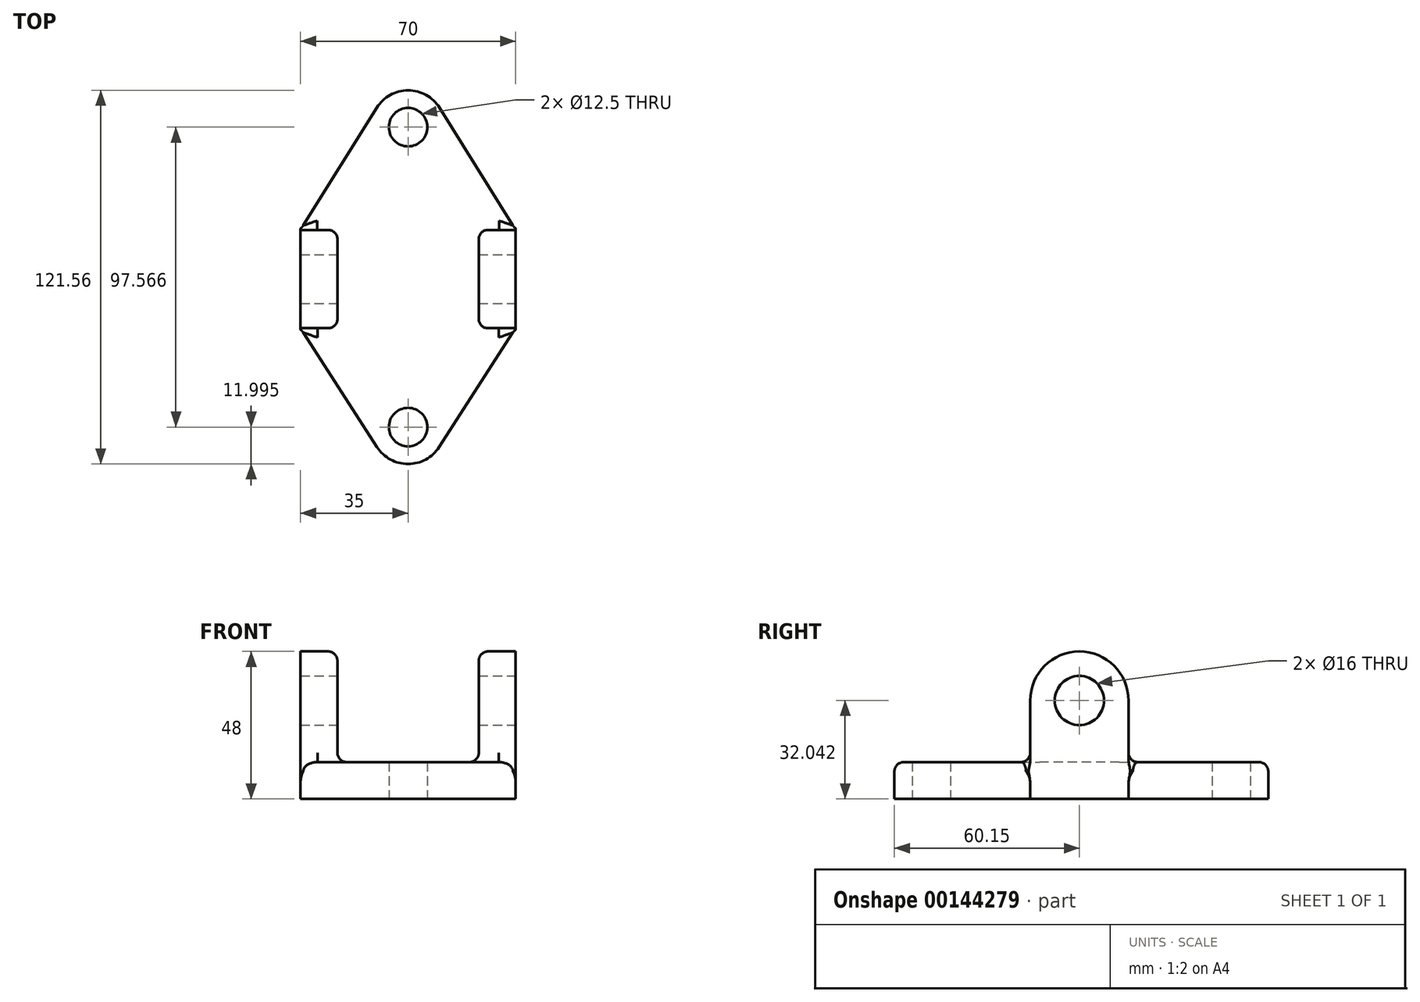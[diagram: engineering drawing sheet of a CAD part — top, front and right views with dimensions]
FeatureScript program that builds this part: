
annotation { "Feature Type Name" : "Feature", "Feature Type Description" : "" }
export const myFeature = defineFeature(function(context is Context, id is Id, definition is map)
    precondition{}
    {
        {
            var Q0;
            Q0=qCreatedBy(makeId("Right.planeOp"),FACE);
            var sketch = newSketch(context, id + "F0", { "sketchPlane" : qUnion([Q0])});
            skLineSegment(sketch, "E0", {"start": v(-16, 0) * mm, "end": v(-16, 32) * mm});
            skLineSegment(sketch, "E1", {"start": v(-16, 0) * mm, "end": v(16, 0) * mm});
            skLineSegment(sketch, "E2", {"start": v(16, 0) * mm, "end": v(16, 32) * mm});
            skCircle(sketch, "E3", {"center": v(0, 32) * mm, "radius": 6 * mm});
            skArc(sketch, "E4", {"start": v(16, 32) * mm, "mid": v(0, 48) * mm, "end": v(-16, 32) * mm});
            skSolve(sketch);
        }
        {
            var Q0;
            Q0 = qSketchRegion(id + "F0", true);
            extrude(context, id + "F1", {"entities" : qUnion([Q0]), "oppositeDirection" : true, "depth" : 12 * mm});
        }
        {
            var Q0;
            Q0=qCreatedBy(makeId("Top.planeOp"),FACE);
            var sketch = newSketch(context, id + "F2", { "sketchPlane" : qUnion([Q0])});
            skPoint(sketch, "E5.0", {"position": v(-12, 16) * mm});
            skPoint(sketch, "E6.0", {"position": v(-12, -16) * mm});
            skCircle(sketch, "E7", {"center": v(23, 49.41) * mm, "radius": 6.25 * mm});
            skArc(sketch, "E8", {"start": v(33.18, 55.77) * mm, "mid": v(23, 61.41) * mm, "end": v(12.82, 55.77) * mm});
            skLineSegment(sketch, "E9", {"start": v(33.18, 55.77) * mm, "end": v(58, 16) * mm});
            skPoint(sketch, "E10", {"position": v(-12, 0) * mm});
            skPoint(sketch, "E11", {"position": v(58, 0) * mm});
            skLineSegment(sketch, "E12", {"start": v(58, 0) * mm, "end": v(58, -16) * mm});
            skLineSegment(sketch, "E13", {"start": v(58, -16) * mm, "end": v(58, 16) * mm});
            skPoint(sketch, "E14", {"position": v(23, 0) * mm});
            skLineSegment(sketch, "E15", {"start": v(23, 74.76) * mm, "end": v(23, -48.15) * mm, "construction": true});
            skLineSegment(sketch, "E16", {"start": v(-12, 16) * mm, "end": v(12.82, 55.77) * mm});
            skCircle(sketch, "E17", {"center": v(23, -48.15) * mm, "radius": 6.25 * mm});
            skArc(sketch, "E18", {"start": v(12.91, -54.66) * mm, "mid": v(23, -60.15) * mm, "end": v(33.09, -54.66) * mm});
            skLineSegment(sketch, "E19", {"start": v(58, -16) * mm, "end": v(33.09, -54.66) * mm});
            skLineSegment(sketch, "E20", {"start": v(12.91, -54.66) * mm, "end": v(-12, -16) * mm});
            skLineSegment(sketch, "E21", {"start": v(-12, -16) * mm, "end": v(-12, 16) * mm});
            skSolve(sketch);
        }
        {
            var Q0;
            Q0 = qSketchRegion(id + "F2", true);
            extrude(context, id + "F3", {"entities" : qUnion([Q0]), "operationType" : NewBodyOperationType.ADD, "depth" : 12 * mm});
        }
        {
            var Q0;
            Q0=makeQuery(id+"F3.opExtrude","SWEPT_FACE",FACE,{"disambiguationData":[OSD([sQuery(id+"F2.wireOp",EDGE,"E13")])]});
            var sketch = newSketch(context, id + "F4", { "sketchPlane" : qUnion([Q0])});
            skLineSegment(sketch, "E22.0.0", {"start": v(-16, 0) * mm, "end": v(-16, 12) * mm});
            skLineSegment(sketch, "E22.0.1", {"start": v(-16, 12) * mm, "end": v(-16, 32) * mm});
            skArc(sketch, "E22.0.2", {"start": v(-16, 32) * mm, "mid": v(0, 48) * mm, "end": v(16, 32) * mm});
            skLineSegment(sketch, "E22.0.3", {"start": v(16, 32) * mm, "end": v(16, 12) * mm});
            skLineSegment(sketch, "E22.0.4", {"start": v(16, 12) * mm, "end": v(16, 0) * mm});
            skLineSegment(sketch, "E22.0.5", {"start": v(16, 0) * mm, "end": v(-16, 0) * mm});
            skCircle(sketch, "E23.0", {"center": v(0, 32) * mm, "radius": 6 * mm});
            skSolve(sketch);
        }
        {
            var Q0;
            Q0 = qSketchRegion(id + "F4", true);
            extrude(context, id + "F5", {"entities" : qUnion([Q0]), "operationType" : NewBodyOperationType.ADD, "oppositeDirection" : true, "depth" : 12 * mm});
        }
        {
            var Q0;
            Q0=makeQuery(id+"F3.opExtrude","CAP_EDGE",EDGE,{"disambiguationData":[OSD([sQuery(id+"F2.wireOp",EDGE,"E19")])],"isStart":false});
            var Q1;
            Q1=makeQuery(id+"F3.opExtrude","CAP_EDGE",EDGE,{"disambiguationData":[OSD([sQuery(id+"F2.wireOp",EDGE,"E9")])],"isStart":false});
            var Q2;
            Q2=makeQuery(id+"F5.opExtrude","CAP_EDGE",EDGE,{"disambiguationData":[OSD([sQuery(id+"F4.wireOp",EDGE,"E22.0.2")])],"isStart":false});
            var Q3;
            Q3=makeQuery(id+"F1.opExtrude","CAP_EDGE",EDGE,{"disambiguationData":[OSD([sQuery(id+"F0.wireOp",EDGE,"E4")])],"isStart":true});
            fillet(context, id + "F6", {"entities" : qUnion([Q0, Q1, Q2, Q3]), "radius" : 3 * mm, "tangentPropagation" : true, "allowEdgeOverflow" : false});
        }
        {
            var Q0;
            Q0=makeQuery(id+"F5.boolean.opBoolean","INTERSECT",EDGE,{"derivedFrom":[makeQuery(id+"F3.opExtrude","CAP_FACE",FACE,{"disambiguationData":[OSD([sQuery(id+"F2.wireOp",EDGE,"E7"),sQuery(id+"F2.wireOp",EDGE,"E8"),sQuery(id+"F2.wireOp",EDGE,"E9"),sQuery(id+"F2.wireOp",EDGE,"E13"),sQuery(id+"F2.wireOp",EDGE,"E16"),sQuery(id+"F2.wireOp",EDGE,"E17"),sQuery(id+"F2.wireOp",EDGE,"E18"),sQuery(id+"F2.wireOp",EDGE,"E19"),sQuery(id+"F2.wireOp",EDGE,"E20"),sQuery(id+"F2.wireOp",EDGE,"E21")])],"isStart":false}),makeQuery(id+"F5.opExtrude","SWEPT_FACE",FACE,{"disambiguationData":[OSD([sQuery(id+"F4.wireOp",EDGE,"E22.0.0"),sQuery(id+"F4.wireOp",EDGE,"E22.0.1")])]})]});
            var Q1;
            Q1=makeQuery(id+"F3.boolean.opBoolean","INTERSECT",EDGE,{"derivedFrom":[makeQuery(id+"F1.opExtrude","SWEPT_FACE",FACE,{"disambiguationData":[OSD([sQuery(id+"F0.wireOp",EDGE,"E0")])]}),makeQuery(id+"F3.opExtrude","CAP_FACE",FACE,{"disambiguationData":[OSD([sQuery(id+"F2.wireOp",EDGE,"E7"),sQuery(id+"F2.wireOp",EDGE,"E8"),sQuery(id+"F2.wireOp",EDGE,"E9"),sQuery(id+"F2.wireOp",EDGE,"E13"),sQuery(id+"F2.wireOp",EDGE,"E16"),sQuery(id+"F2.wireOp",EDGE,"E17"),sQuery(id+"F2.wireOp",EDGE,"E18"),sQuery(id+"F2.wireOp",EDGE,"E19"),sQuery(id+"F2.wireOp",EDGE,"E20"),sQuery(id+"F2.wireOp",EDGE,"E21")])],"isStart":false})]});
            fillet(context, id + "F7", {"entities" : qUnion([Q0, Q1]), "radius" : 3 * mm, "tangentPropagation" : true, "allowEdgeOverflow" : false});
        }
        {
            var Q0;
            Q0=makeQuery(id+"F4.imprint","IMPRINT",FACE,{"disambiguationData":[TD([[makeQuery(id+"F4.imprint","IMPRINT",EDGE,{"derivedFrom":sQuery(id+"F4.wireOp",EDGE,"E22.0.1")}),-1.0]])]});
            var sketch = newSketch(context, id + "F8", { "sketchPlane" : qUnion([Q0])});
            skCircle(sketch, "E24", {"center": v(0, 32.04) * mm, "radius": 8 * mm});
            skLineSegment(sketch, "E25", {"start": v(-12.88, 17) * mm, "end": v(13.25, 17) * mm});
            skLineSegment(sketch, "E26", {"start": v(13.25, 17) * mm, "end": v(10.48, 42.4) * mm});
            skLineSegment(sketch, "E27", {"start": v(10.48, 42.4) * mm, "end": v(-7.83, 42.4) * mm});
            skLineSegment(sketch, "E28", {"start": v(-7.83, 42.4) * mm, "end": v(-12.88, 17) * mm});
            skSolve(sketch);
        }
        {
            var Q0;
            Q0=makeQuery(id+"F8.imprint","IMPRINT",FACE,{"disambiguationData":[TD([[makeQuery(id+"F8.imprint","IMPRINT",EDGE,{"derivedFrom":sQuery(id+"F8.wireOp",EDGE,"E24")}),1.0]])]});
            extrude(context, id + "F9", {"entities" : qUnion([Q0]), "operationType" : NewBodyOperationType.REMOVE, "endBound" : BoundingType.THROUGH_ALL, "oppositeDirection" : true, "depth" : 25 * mm});
        }
    });
